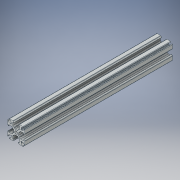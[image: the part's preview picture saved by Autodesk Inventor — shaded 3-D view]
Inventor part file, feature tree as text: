
AUTODESK INVENTOR PART (.ipt)
format: ipt  version: 2016 (Build 200138000, 138)  size: 361,472 bytes
history: native  units: in
note: dims shown in document units (in); Inventor stores cm internally (conversion verified against a paired STEP export)
features: extrude x1, sketch x1, fillet x1
ambient origin geometry x8: Origin, YZ Plane, XZ Plane, XY Plane, X Axis, Y Axis, Z Axis, Center Point
bodies: Solid1 (feature_tree)
feature tree (3):
  extrude  "Extrusion1"  [1 undecoded]
  sketch  "Sketch1"  dims[d0=63.5in d1=0.0in]
  fillet  "Fillet10"  [1 undecoded]
note: 2 required parameter values undecoded (feature->parameter linkage not recoverable at this tier; creation-order binding heuristic only, values carry confidence <= 0.55)
